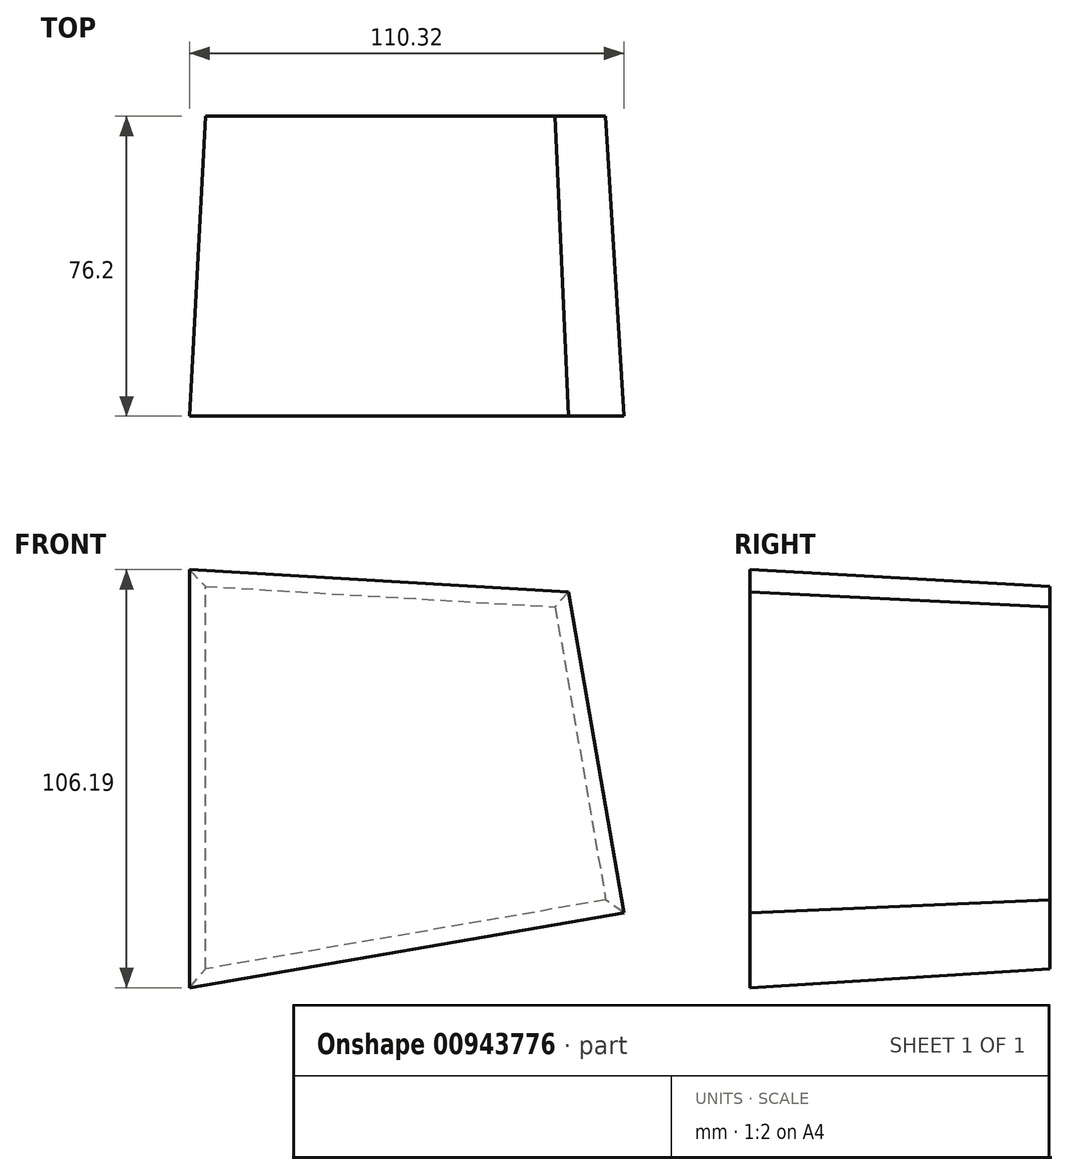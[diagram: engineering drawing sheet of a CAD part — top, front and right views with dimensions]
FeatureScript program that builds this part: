
annotation { "Feature Type Name" : "Feature", "Feature Type Description" : "" }
export const myFeature = defineFeature(function(context is Context, id is Id, definition is map)
    precondition{}
    {
        {
            var Q0;
            Q0=qCreatedBy(makeId("Front.planeOp"),FACE);
            var sketch = newSketch(context, id + "F0", { "sketchPlane" : qUnion([Q0])});
            skLineSegment(sketch, "E0", {"start": v(63.48, 74.46) * mm, "end": v(76.33, 0) * mm});
            skLineSegment(sketch, "E1", {"start": v(76.33, 0) * mm, "end": v(-25.38, -17.56) * mm});
            skLineSegment(sketch, "E2", {"start": v(-25.38, -17.56) * mm, "end": v(-25.38, 79.66) * mm});
            skLineSegment(sketch, "E3", {"start": v(-25.38, 79.66) * mm, "end": v(63.48, 74.46) * mm});
            skSolve(sketch);
        }
        {
            var Q0;
            Q0 = qSketchRegion(id + "F0", true);
            extrude(context, id + "F1", {"entities" : qUnion([Q0]), "depth" : 76.2 * mm, "offsetDistance" : 25.4 * mm, "hasDraft" : true, "draftAngle" : 3 * degree});
        }
    });
